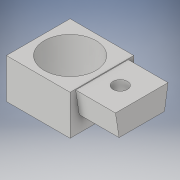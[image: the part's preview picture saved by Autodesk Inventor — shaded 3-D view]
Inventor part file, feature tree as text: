
AUTODESK INVENTOR PART (.ipt)
format: ipt  version: 2018 (Build 220112000, 112)  size: 122,880 bytes
history: native  units: in
note: dims shown in document units (in); Inventor stores cm internally (conversion verified against a paired STEP export)
features: extrude x3, sketch x3
ambient origin geometry x8: Origin, YZ Plane, XZ Plane, XY Plane, X Axis, Y Axis, Z Axis, Center Point
bodies: Solid1 (feature_tree)
feature tree (6):
  extrude  "Extrusion1"  Depth=0.8in
  extrude  "Extrusion2"  Depth=0.4in
  extrude  "Extrusion3"  Depth=0.5in TaperAngle=0.0deg
  sketch  "Sketch1"  dims[d0=0.8in d1=0.8in]
  sketch  "Sketch2"  dims[d2=0.4in d3=0.4in]
  sketch  "Sketch3"  dims[d4=0.65in d5=0.5in d6=0.0in d7=0.66in d8=0.57in d9=0.29in d10=0.2in d11=0.115in d12=0.5in d13=0.0in d14=0.18in d15=0.27in d16=0.7in d17=0.0in]
